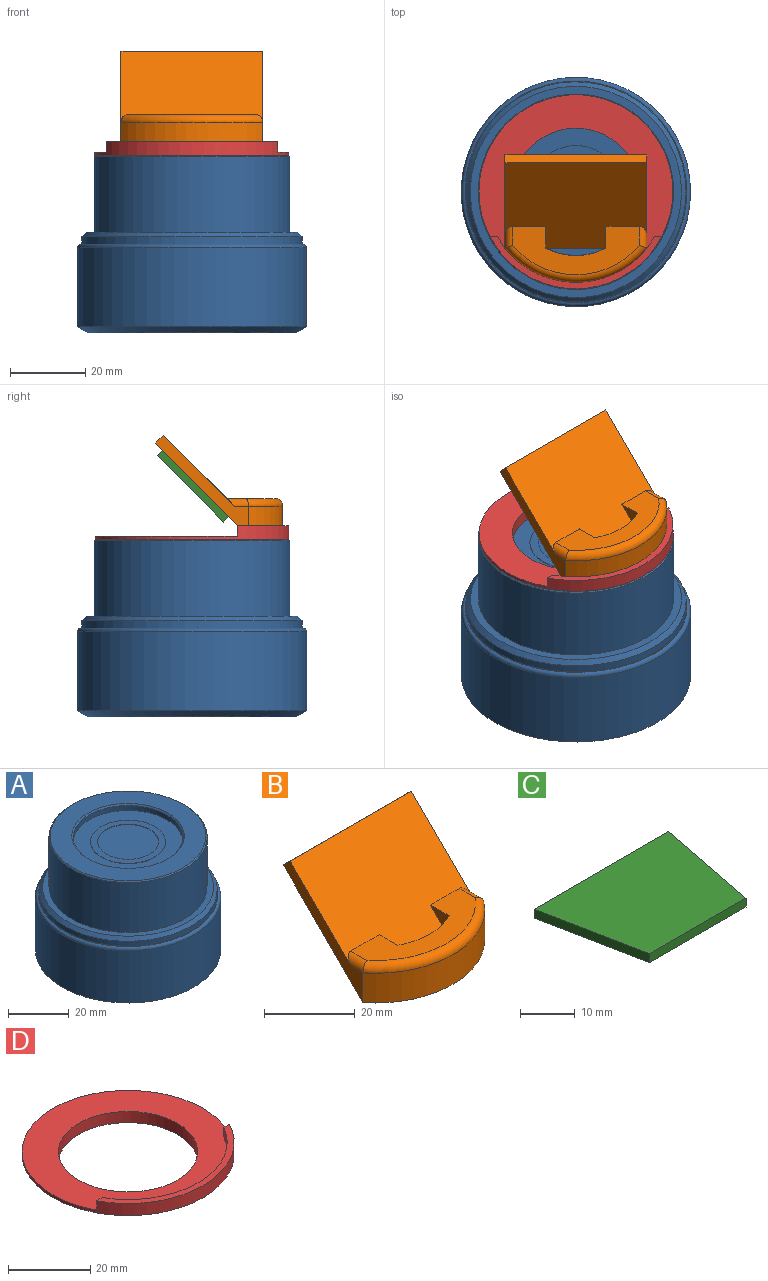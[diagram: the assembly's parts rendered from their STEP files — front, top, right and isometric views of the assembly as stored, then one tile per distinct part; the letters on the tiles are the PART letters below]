
ASSEMBLY  parts=4 mates=5
PART A: 18 faces, bbox 66x66x47.3 mm
  f0: cylinder r=30.5mm len=61mm, axis (0,0,-1), area 4024.4mm2, adj f6,f7
  f1: plane 59x59mm, normal (0,0,1), area 36.9mm2, adj f3,f6
  f2: plane 55x55mm, normal (0,0,-1), area 2375.8mm2, adj f7
  f3: cylinder r=29.3mm len=58.6mm, axis (0,0,-1), area 368.2mm2, adj f1,f5
  f4: plane 56.2x56.2mm, normal (0,0,1), area 356.9mm2, adj f5,f8
  f5: cone r=28.1mm half-angle=45deg, axis (0,0,-1), area 306mm2, adj f3,f4
  f6: torus R=29.5mm, axis (0,0,1), area 297.4mm2, adj f0,f1
  f7: cone r=30.5mm half-angle=61.9deg, axis (0,0,1), area 619.5mm2, adj f0,f2
  f8: cylinder r=26mm len=52mm, axis (0,0,-1), area 3283.6mm2, adj f4,f17
  f9: plane 51.2x51.2mm, normal (0,0,1), area 983.7mm2, adj f16,f17
  f10: cylinder r=18mm len=36mm, axis (0,0,1), area 226.2mm2, adj f11,f16
  f11: plane 36x36mm, normal (0,0,1), area 542.6mm2, adj f10,f12
  f12: cylinder r=12.3mm len=24.6mm, axis (0,0,-1), area 11.6mm2, adj f11,f13
  f13: plane 24.6x24.6mm, normal (0,0,1), area 161.1mm2, adj f12,f14
  f14: cylinder r=10mm len=20mm, axis (0,0,1), area 9.4mm2, adj f13,f15
  f15: plane 20x20mm, normal (0,0,1), area 314.2mm2, adj f14
  f16: cone r=18mm half-angle=45deg, axis (0,0,1), area 81.1mm2, adj f9,f10
  f17: cone r=25.6mm half-angle=45deg, axis (0,0,-1), area 91.7mm2, adj f8,f9
PART B: 15 faces, bbox 40.8x35.8x26.9 mm
  f0: cylinder r=24.1mm len=37.73mm, axis (0,0,-1), area 346.6mm2, adj f3,f5,f9,f13
  f1: cylinder r=17mm len=16mm, axis (0,0,-1), area 166.6mm2, adj f2,f3,f4,f10,f11
  f2: plane 33.73x12.86mm, normal (0,0,1), area 239.4mm2, adj f1,f8,f10,f11,f12,f13,f14
  f3: plane 37.73x9.1mm, normal (0,0,-1), area 217.6mm2, adj f0,f1,f6
  f4: plane 16x4.24mm, normal (0,-1,0), area 67.9mm2, adj f1,f6,f8
  f5: plane 26.87x24.75mm, normal (1,0,0), area 107.6mm2, adj f0,f6,f7,f8,f12
  f6: plane 37.73x24.75mm, normal (0,0.71,-0.71), area 1320.4mm2, adj f3,f4,f5,f7,f9
  f7: plane 37.73x2.12mm, normal (0,0.71,0.71), area 113.2mm2, adj f5,f6,f8,f9
  f8: plane 37.73x22.63mm, normal (0,-0.71,0.71), area 1032.8mm2, adj f2,f4,f5,f7,f9,f10,f11,f12
  f9: plane 26.87x24.75mm, normal (-1,0,0), area 107.6mm2, adj f0,f6,f7,f8,f14
  f10: plane 5.76x5.76mm, normal (1,0,0), area 16.6mm2, adj f1,f2,f8
  f11: plane 5.76x5.76mm, normal (-1,0,0), area 16.6mm2, adj f1,f2,f8
  f12: cylinder r=2mm len=5.76mm, axis (0,-1,0), area 15mm2, adj f2,f5,f8,f13
  f13: torus R=22.1mm, axis (0,0,1), area 130.4mm2, adj f0,f2,f12,f14
  f14: cylinder r=2mm len=5.76mm, axis (0,1,0), area 15mm2, adj f2,f8,f9,f13
PART C: 6 faces, bbox 35x25x2 mm
  f0: plane 25x5mm, normal (-0.98,-0.2,0), area 51mm2, adj f1,f3,f4,f5
  f1: plane 25x2mm, normal (0,-1,0), area 50mm2, adj f0,f2,f4,f5
  f2: plane 25x5mm, normal (0.98,-0.2,0), area 51mm2, adj f1,f3,f4,f5
  f3: plane 35x2mm, normal (0,1,0), area 70mm2, adj f0,f2,f4,f5
  f4: plane 35x25mm, normal (0,0,1), area 750mm2, adj f0,f1,f2,f3
  f5: plane 35x25mm, normal (0,0,-1), area 750mm2, adj f0,f1,f2,f3
PART D: 10 faces, bbox 51.6x51.6x6.1 mm
  f0: cylinder r=25.8mm len=51.6mm, axis (0,0,-1), area 286.7mm2, adj f2,f3,f4,f6,f7
  f1: cylinder r=24.1mm len=41.8mm, axis (0,0,-1), area 141.7mm2, adj f3,f4,f6,f7
  f2: plane 51.6x51.6mm, normal (0,0,-1), area 1027.6mm2, adj f0,f8
  f3: plane 45.68x13.8mm, normal (0,0,1), area 90.7mm2, adj f0,f1,f6,f7
  f4: plane 51.6x49.9mm, normal (0,0,1), area 1099mm2, adj f0,f1,f5,f6,f7
  f5: cylinder r=16.94mm len=33.88mm, axis (0,0,1), area 351.2mm2, adj f4,f9
  f6: plane 2.8x1.94mm, normal (0,1,0), area 5.4mm2, adj f0,f1,f3,f4
  f7: plane 2.8x1.94mm, normal (0,1,0), area 5.4mm2, adj f0,f1,f3,f4
  f8: cylinder r=18.4mm len=36.8mm, axis (0,0,1), area 289mm2, adj f2,f9
  f9: plane 36.8x36.8mm, normal (0,0,-1), area 162.1mm2, adj f5,f8
PLACE A t=(0,2.06,-49.24)mm
PLACE B t=(0,2.06,-1.14)mm
PLACE C rot(axis=(1,0,0),45deg) t=(-12.19,-6.38,2.6)mm
PLACE D t=(0,2.06,-1.94)mm
MATE planar D.f1 <-> A.f12  axis (0,0,-1) through (0,2.06,-1.94)mm
MATE cylindrical D.f5 <-> A.f10  axis (0,0,1) through (0,2.06,-2.79)mm
MATE planar B.f3 <-> D.f4  axis (0,0,-1) through (0,-16.94,-1.14)mm
MATE cylindrical D.f1 <-> B.f0  axis (0,0,-1) through (0,2.06,0.26)mm
MATE planar C.f4 <-> B.f6  axis (0,-0.71,0.71) through (0.31,1.54,13.34)mm
